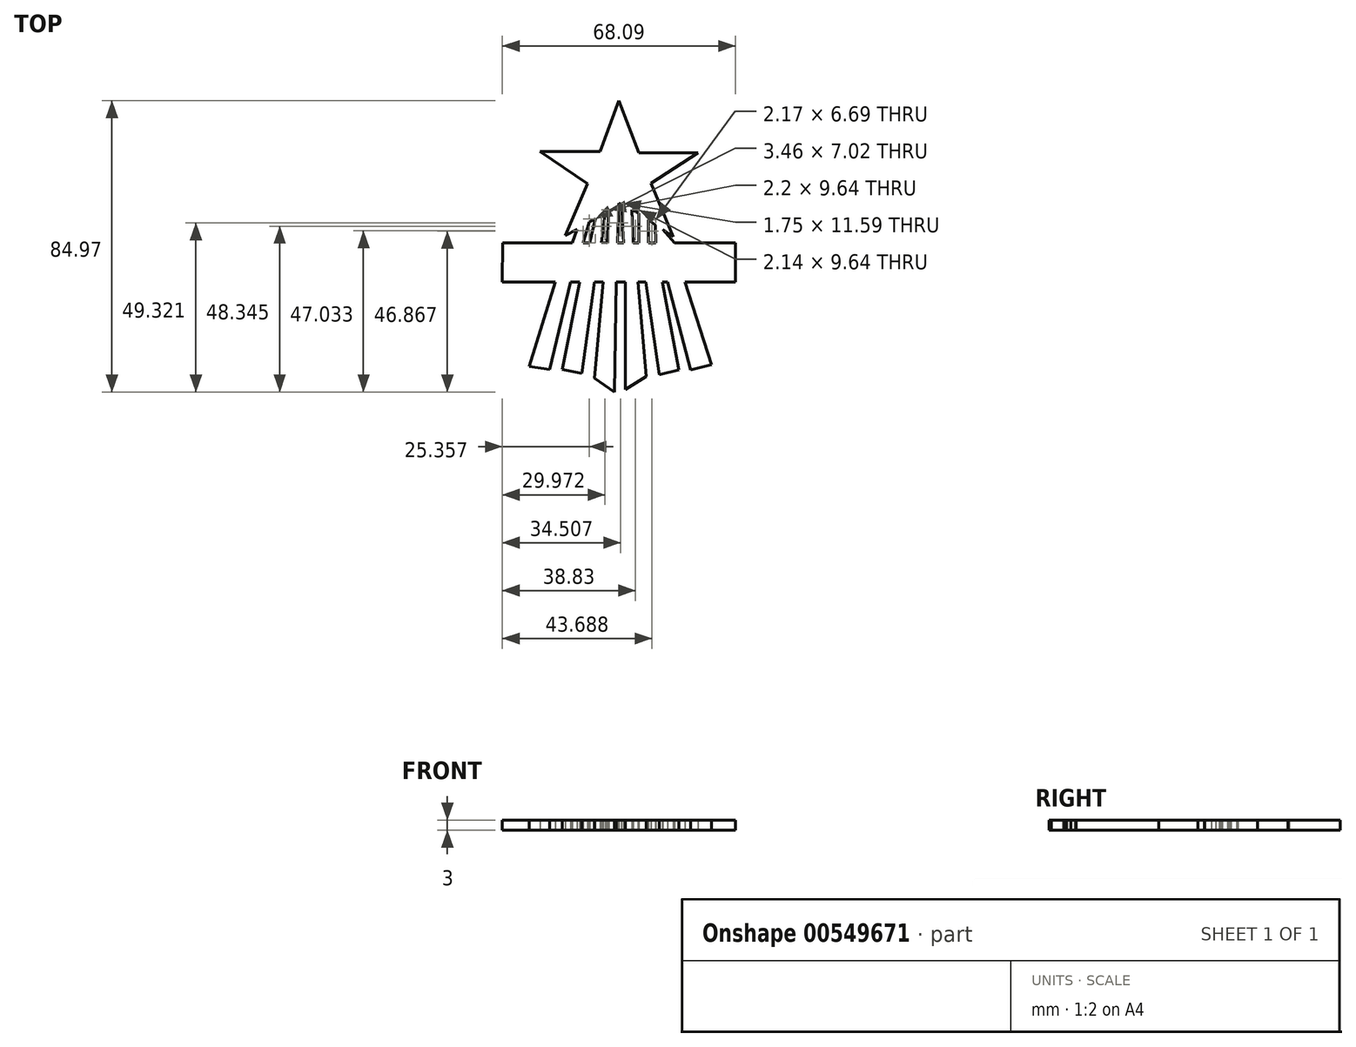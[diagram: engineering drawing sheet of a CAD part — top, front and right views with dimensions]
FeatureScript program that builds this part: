
annotation { "Feature Type Name" : "Feature", "Feature Type Description" : "" }
export const myFeature = defineFeature(function(context is Context, id is Id, definition is map)
    precondition{}
    {
        {
            var Q0;
            Q0=qCreatedBy(makeId("Top.planeOp"),FACE);
            var sketch = newSketch(context, id + "F0", { "sketchPlane" : qUnion([Q0])});
            skLineSegment(sketch, "E0", {"start": v(-118.8, 11.65) * mm, "end": v(-124.31, -3.15) * mm});
            skLineSegment(sketch, "E1", {"start": v(-124.31, -3.15) * mm, "end": v(-141.8, -3.15) * mm});
            skLineSegment(sketch, "E2", {"start": v(-141.8, -3.15) * mm, "end": v(-127.88, -12.57) * mm});
            skLineSegment(sketch, "E3", {"start": v(-127.88, -12.57) * mm, "end": v(-134.47, -27.71) * mm});
            skLineSegment(sketch, "E4", {"start": v(-134.47, -27.71) * mm, "end": v(-130.97, -25.9) * mm});
            skLineSegment(sketch, "E5", {"start": v(-130.97, -25.9) * mm, "end": v(-132.39, -29.8) * mm});
            skLineSegment(sketch, "E6", {"start": v(-132.39, -29.8) * mm, "end": v(-152.7, -29.8) * mm});
            skLineSegment(sketch, "E7", {"start": v(-84.75, -29.8) * mm, "end": v(-102.53, -29.8) * mm});
            skLineSegment(sketch, "E8", {"start": v(-102.53, -29.8) * mm, "end": v(-105.98, -25.9) * mm});
            skLineSegment(sketch, "E9", {"start": v(-105.98, -25.9) * mm, "end": v(-102.96, -28) * mm});
            skLineSegment(sketch, "E10", {"start": v(-102.96, -28) * mm, "end": v(-109.34, -12.4) * mm});
            skLineSegment(sketch, "E11", {"start": v(-109.34, -12.4) * mm, "end": v(-95.64, -3.54) * mm});
            skLineSegment(sketch, "E12", {"start": v(-95.64, -3.54) * mm, "end": v(-112.96, -3.54) * mm});
            skLineSegment(sketch, "E13", {"start": v(-112.96, -3.54) * mm, "end": v(-118.8, 11.65) * mm});
            skLineSegment(sketch, "E14", {"start": v(-110.2, -23.11) * mm, "end": v(-110.2, -29.8) * mm});
            skLineSegment(sketch, "E15", {"start": v(-110.2, -29.8) * mm, "end": v(-108.03, -29.8) * mm});
            skLineSegment(sketch, "E16", {"start": v(-108.03, -29.8) * mm, "end": v(-108.19, -24.6) * mm});
            skLineSegment(sketch, "E17", {"start": v(-108.19, -24.6) * mm, "end": v(-110.2, -23.11) * mm});
            skLineSegment(sketch, "E18", {"start": v(-115.04, -20.15) * mm, "end": v(-112.9, -21.2) * mm});
            skLineSegment(sketch, "E19", {"start": v(-112.9, -21.2) * mm, "end": v(-112.9, -29.8) * mm});
            skLineSegment(sketch, "E20", {"start": v(-112.9, -29.8) * mm, "end": v(-114.56, -29.8) * mm});
            skLineSegment(sketch, "E21", {"start": v(-114.56, -29.8) * mm, "end": v(-115.04, -20.15) * mm});
            skLineSegment(sketch, "E22", {"start": v(-118.8, -18.2) * mm, "end": v(-117.98, -18.5) * mm});
            skLineSegment(sketch, "E23", {"start": v(-117.98, -18.5) * mm, "end": v(-117.42, -29.8) * mm});
            skLineSegment(sketch, "E24", {"start": v(-117.42, -29.8) * mm, "end": v(-119.17, -29.8) * mm});
            skLineSegment(sketch, "E25", {"start": v(-119.17, -29.8) * mm, "end": v(-118.8, -18.2) * mm});
            skLineSegment(sketch, "E26", {"start": v(-122.75, -20.68) * mm, "end": v(-121.73, -20.15) * mm});
            skLineSegment(sketch, "E27", {"start": v(-121.73, -20.15) * mm, "end": v(-122.22, -29.8) * mm});
            skLineSegment(sketch, "E28", {"start": v(-122.22, -29.8) * mm, "end": v(-123.93, -29.7) * mm});
            skLineSegment(sketch, "E29", {"start": v(-123.93, -29.7) * mm, "end": v(-122.75, -20.68) * mm});
            skLineSegment(sketch, "E30", {"start": v(-127.46, -23.67) * mm, "end": v(-125.72, -22.78) * mm});
            skLineSegment(sketch, "E31", {"start": v(-125.72, -22.78) * mm, "end": v(-127.32, -29.8) * mm});
            skLineSegment(sketch, "E32", {"start": v(-127.32, -29.8) * mm, "end": v(-129.17, -29.8) * mm});
            skLineSegment(sketch, "E33", {"start": v(-129.17, -29.8) * mm, "end": v(-127.46, -23.67) * mm});
            skLineSegment(sketch, "E34", {"start": v(-152.8, -41.23) * mm, "end": v(-137.32, -41.23) * mm});
            skLineSegment(sketch, "E35", {"start": v(-137.32, -41.23) * mm, "end": v(-145, -65.86) * mm});
            skLineSegment(sketch, "E36", {"start": v(-132.88, -41.23) * mm, "end": v(-130.18, -41.23) * mm});
            skLineSegment(sketch, "E37", {"start": v(-130.18, -41.23) * mm, "end": v(-135.29, -66.76) * mm});
            skLineSegment(sketch, "E38", {"start": v(-135.29, -66.76) * mm, "end": v(-138.93, -66.76) * mm});
            skLineSegment(sketch, "E39", {"start": v(-138.93, -66.76) * mm, "end": v(-132.88, -41.23) * mm});
            skLineSegment(sketch, "E40", {"start": v(-125.89, -41.23) * mm, "end": v(-123.34, -41.23) * mm});
            skLineSegment(sketch, "E41", {"start": v(-123.34, -41.23) * mm, "end": v(-125.87, -69.32) * mm});
            skLineSegment(sketch, "E42", {"start": v(-125.87, -69.32) * mm, "end": v(-129.55, -67.97) * mm});
            skLineSegment(sketch, "E43", {"start": v(-129.55, -67.97) * mm, "end": v(-125.89, -41.23) * mm});
            skLineSegment(sketch, "E44", {"start": v(-119.62, -41.23) * mm, "end": v(-116.95, -41.23) * mm});
            skLineSegment(sketch, "E45", {"start": v(-116.95, -41.23) * mm, "end": v(-116.95, -72.58) * mm});
            skLineSegment(sketch, "E46", {"start": v(-116.95, -72.58) * mm, "end": v(-118.53, -74.9) * mm});
            skLineSegment(sketch, "E47", {"start": v(-118.53, -74.9) * mm, "end": v(-120.08, -73.32) * mm});
            skLineSegment(sketch, "E48", {"start": v(-120.08, -73.32) * mm, "end": v(-119.62, -41.23) * mm});
            skLineSegment(sketch, "E49", {"start": v(-113.19, -41.23) * mm, "end": v(-110.9, -41.23) * mm});
            skLineSegment(sketch, "E50", {"start": v(-110.9, -41.23) * mm, "end": v(-106.96, -68.3) * mm});
            skLineSegment(sketch, "E51", {"start": v(-106.96, -68.3) * mm, "end": v(-110.73, -68.84) * mm});
            skLineSegment(sketch, "E52", {"start": v(-110.73, -68.84) * mm, "end": v(-113.19, -41.23) * mm});
            skLineSegment(sketch, "E53", {"start": v(-106.15, -41.23) * mm, "end": v(-104.62, -41.23) * mm});
            skLineSegment(sketch, "E54", {"start": v(-104.62, -41.23) * mm, "end": v(-97.83, -66.87) * mm});
            skLineSegment(sketch, "E55", {"start": v(-97.83, -66.87) * mm, "end": v(-101.25, -66.87) * mm});
            skLineSegment(sketch, "E56", {"start": v(-101.25, -66.87) * mm, "end": v(-106.15, -41.23) * mm});
            skLineSegment(sketch, "E57", {"start": v(-99.48, -41.23) * mm, "end": v(-91.78, -65.37) * mm});
            skLineSegment(sketch, "E58", {"start": v(-84.71, -41.23) * mm, "end": v(-99.48, -41.23) * mm});
            skLineSegment(sketch, "E59", {"start": v(-91.78, -65.37) * mm, "end": v(-97.83, -66.87) * mm});
            skLineSegment(sketch, "E60", {"start": v(-101.25, -66.87) * mm, "end": v(-106.96, -68.3) * mm});
            skLineSegment(sketch, "E61", {"start": v(-110.73, -68.84) * mm, "end": v(-116.95, -72.58) * mm});
            skLineSegment(sketch, "E62", {"start": v(-120.08, -73.32) * mm, "end": v(-125.87, -69.32) * mm});
            skLineSegment(sketch, "E63", {"start": v(-129.55, -67.97) * mm, "end": v(-135.29, -66.76) * mm});
            skLineSegment(sketch, "E64", {"start": v(-138.93, -66.76) * mm, "end": v(-145, -65.86) * mm});
            skLineSegment(sketch, "E65", {"start": v(-84.75, -29.8) * mm, "end": v(-84.71, -41.23) * mm});
            skLineSegment(sketch, "E66", {"start": v(-152.7, -29.8) * mm, "end": v(-152.8, -41.23) * mm});
            skSolve(sketch);
        }
        {
            var Q0;
            Q0=makeQuery(id+"F0.imprint","IMPRINT",FACE,{"disambiguationData":[TD([[makeQuery(id+"F0.imprint","IMPRINT",EDGE,{"derivedFrom":sQuery(id+"F0.wireOp",EDGE,"E7")}),1.0]])]});
            var Q1;
            {var subQ0=sQuery(id+"F0.wireOp",EDGE,"E1");Q1=makeQuery(id+"F0.imprint","IMPRINT",FACE,{"disambiguationData":[TD([[makeQuery(id+"F0.imprint","IMPRINT",EDGE,{"derivedFrom":subQ0}),1.0]])]});}
            extrude(context, id + "F1", {"entities" : qUnion([Q0, Q1]), "depth" : 3 * mm, "offsetDistance" : 25.4 * mm});
        }
    });
